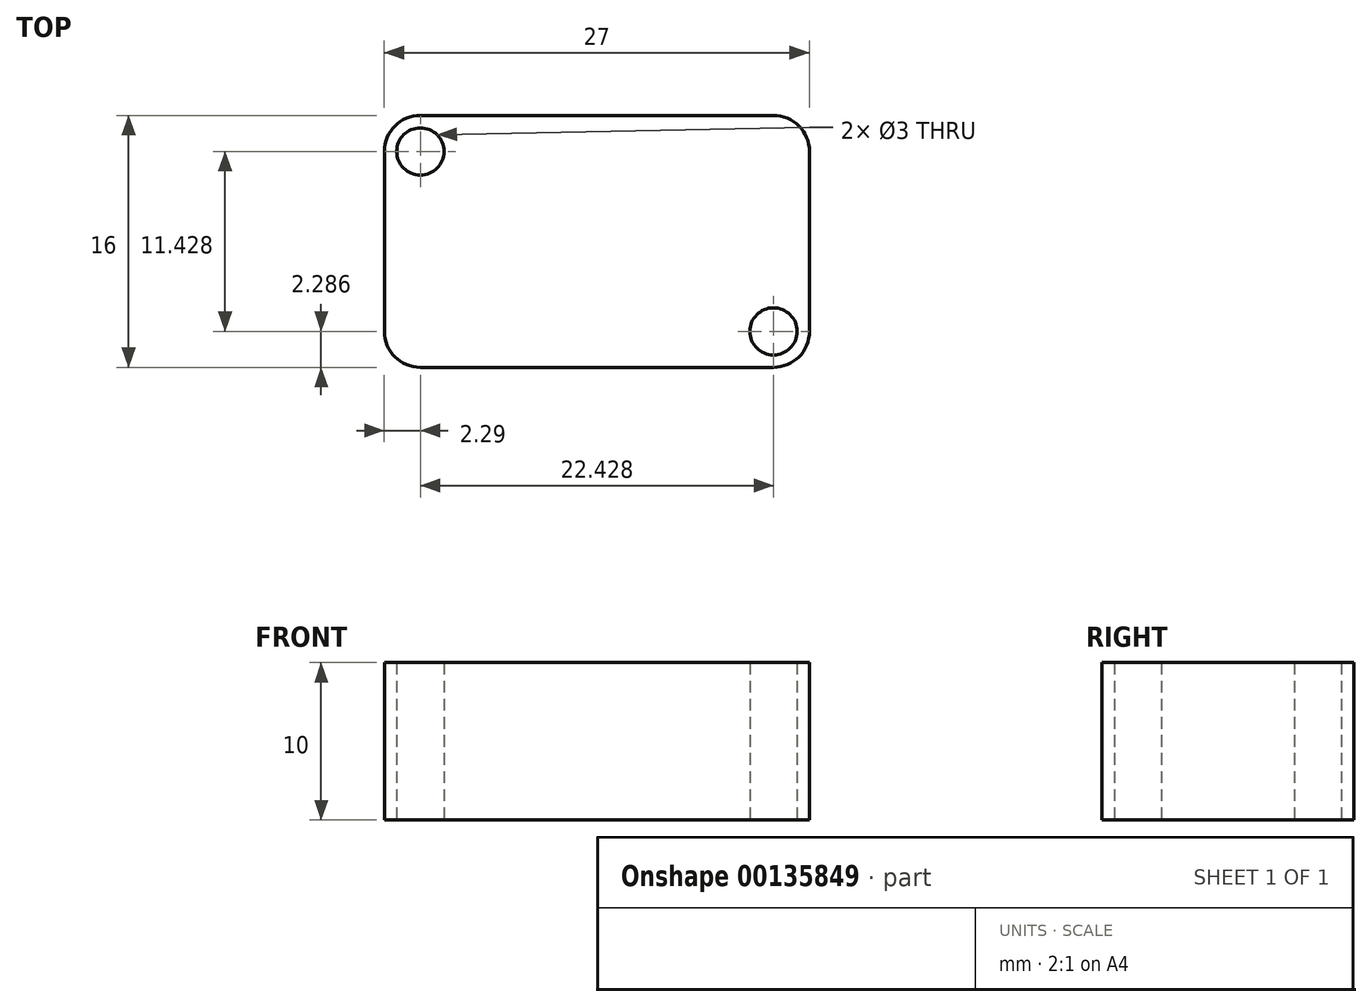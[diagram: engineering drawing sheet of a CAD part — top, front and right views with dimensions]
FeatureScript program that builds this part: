
annotation { "Feature Type Name" : "Feature", "Feature Type Description" : "" }
export const myFeature = defineFeature(function(context is Context, id is Id, definition is map)
    precondition{}
    {
        {
            var Q0;
            Q0=qCreatedBy(makeId("Top.planeOp"),FACE);
            var sketch = newSketch(context, id + "F0", { "sketchPlane" : qUnion([Q0])});
            skLineSegment(sketch, "E0.bottom", {"start": v(-16.65, 0) * mm, "end": v(5.78, 0) * mm});
            skLineSegment(sketch, "E0.top", {"start": v(-16.65, 16) * mm, "end": v(5.78, 16) * mm});
            skLineSegment(sketch, "E0.left", {"start": v(-18.94, 2.29) * mm, "end": v(-18.94, 13.71) * mm});
            skLineSegment(sketch, "E0.right", {"start": v(8.06, 2.29) * mm, "end": v(8.06, 13.71) * mm});
            skPoint(sketch, "E1.visualSharp", {"position": v(8.06, 16) * mm});
            skArc(sketch, "E1.filletArc", {"start": v(8.06, 13.71) * mm, "mid": v(7.4, 15.33) * mm, "end": v(5.78, 16) * mm});
            skPoint(sketch, "E2.visualSharp", {"position": v(-18.94, 16) * mm});
            skArc(sketch, "E2.filletArc", {"start": v(-16.65, 16) * mm, "mid": v(-18.27, 15.33) * mm, "end": v(-18.94, 13.71) * mm});
            skPoint(sketch, "E3.visualSharp", {"position": v(8.06, 0) * mm});
            skArc(sketch, "E3.filletArc", {"start": v(5.78, 0) * mm, "mid": v(7.4, 0.67) * mm, "end": v(8.06, 2.29) * mm});
            skPoint(sketch, "E4.visualSharp", {"position": v(-18.94, 0) * mm});
            skArc(sketch, "E4.filletArc", {"start": v(-18.94, 2.29) * mm, "mid": v(-18.27, 0.67) * mm, "end": v(-16.65, 0) * mm});
            skCircle(sketch, "E5", {"center": v(-16.65, 13.71) * mm, "radius": 1.5 * mm});
            skCircle(sketch, "E6", {"center": v(5.78, 2.29) * mm, "radius": 1.5 * mm});
            skSolve(sketch);
        }
        {
            var Q0;
            Q0 = qSketchRegion(id + "F0", true);
            extrude(context, id + "F1", {"entities" : qUnion([Q0]), "depth" : 10 * mm});
        }
    });
